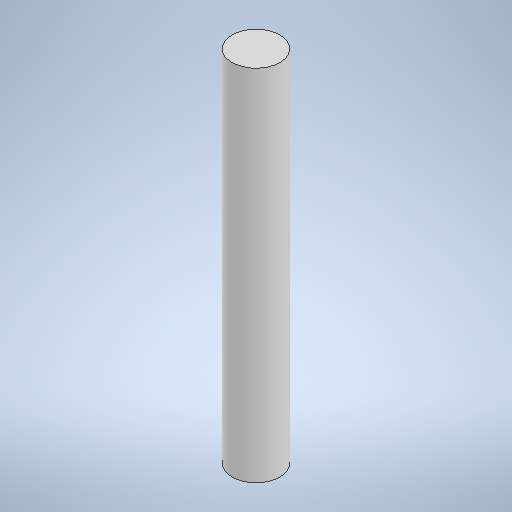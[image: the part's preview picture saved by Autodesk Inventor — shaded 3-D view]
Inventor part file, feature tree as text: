
AUTODESK INVENTOR PART (.ipt)
format: ipt  version: 2025.1 (Build 291241000, 241)  size: 236,544 bytes
history: native  units: mm
features: extrude x1, sketch x1
ambient origin geometry x8: Origin, YZ Plane, XZ Plane, XY Plane, X Axis, Y Axis, Z Axis, Center Point
bodies: Solid1 (feature_tree)
feature tree (2):
  extrude  "Extrusion1"  Depth=22.5mm TaperAngle=0.0deg
  sketch  "Sketch1"  dims[d0=3.0mm d1=22.5mm d2=0.0mm]
